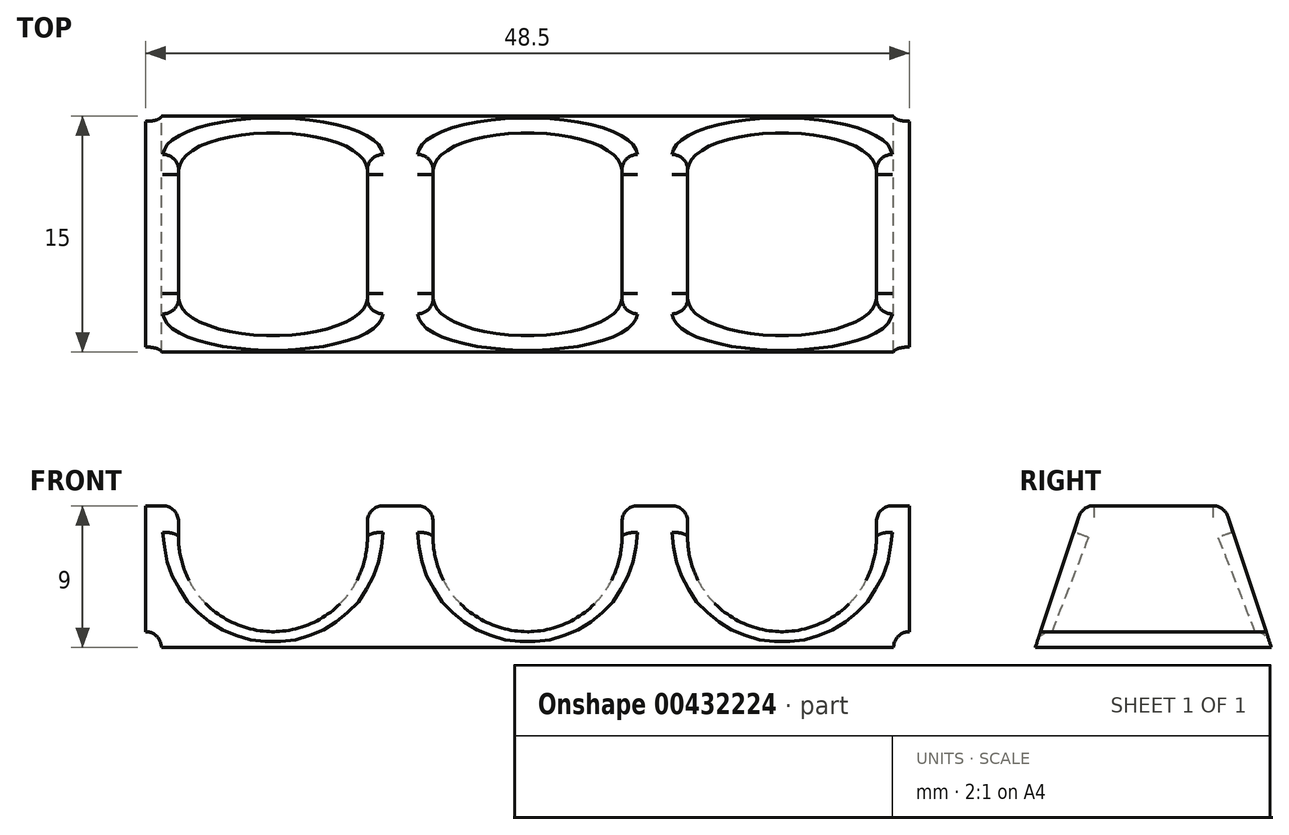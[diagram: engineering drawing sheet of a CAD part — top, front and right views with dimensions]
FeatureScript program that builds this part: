
annotation { "Feature Type Name" : "Feature", "Feature Type Description" : "" }
export const myFeature = defineFeature(function(context is Context, id is Id, definition is map)
    precondition{}
    {
        {
            var Q0;
            Q0=qCreatedBy(makeId("Front.planeOp"),FACE);
            var sketch = newSketch(context, id + "F0", { "sketchPlane" : qUnion([Q0])});
            skLineSegment(sketch, "E0.bottom", {"start": v(24.25, 4.5) * mm, "end": v(22.17, 4.5) * mm});
            skLineSegment(sketch, "E0.top", {"start": v(23.25, -4.5) * mm, "end": v(-23.25, -4.5) * mm});
            skLineSegment(sketch, "E0.left", {"start": v(24.25, 4.5) * mm, "end": v(24.25, -3.5) * mm});
            skLineSegment(sketch, "E0.right", {"start": v(-24.25, 4.5) * mm, "end": v(-24.25, -3.5) * mm});
            skPoint(sketch, "E0.middle", {"position": v(0, 0) * mm});
            skArc(sketch, "E1", {"start": v(-23.25, -4.5) * mm, "mid": v(-23.54, -3.8) * mm, "end": v(-24.25, -3.5) * mm});
            skArc(sketch, "E2", {"start": v(24.25, -3.5) * mm, "mid": v(23.54, -3.8) * mm, "end": v(23.25, -4.5) * mm});
            skArc(sketch, "E3", {"start": v(-22.17, 2.5) * mm, "mid": v(-16.17, -3.5) * mm, "end": v(-10.17, 2.5) * mm});
            skArc(sketch, "E4", {"start": v(10.17, 2.5) * mm, "mid": v(16.17, -3.5) * mm, "end": v(22.17, 2.5) * mm});
            skArc(sketch, "E5", {"start": v(-6, 2.5) * mm, "mid": v(0, -3.5) * mm, "end": v(6, 2.5) * mm});
            skLineSegment(sketch, "E6", {"start": v(-22.17, 2.5) * mm, "end": v(-22.17, 4.5) * mm});
            skLineSegment(sketch, "E7", {"start": v(-10.17, 2.5) * mm, "end": v(-10.17, 4.5) * mm});
            skLineSegment(sketch, "E8", {"start": v(-6, 2.5) * mm, "end": v(-6, 4.5) * mm});
            skLineSegment(sketch, "E9", {"start": v(6, 2.5) * mm, "end": v(6, 4.5) * mm});
            skLineSegment(sketch, "E10", {"start": v(10.17, 2.5) * mm, "end": v(10.17, 4.5) * mm});
            skLineSegment(sketch, "E11", {"start": v(22.17, 2.5) * mm, "end": v(22.17, 4.5) * mm});
            skLineSegment(sketch, "E12.trimOffspring", {"start": v(-22.17, 4.5) * mm, "end": v(-24.25, 4.5) * mm});
            skLineSegment(sketch, "E13.trimOffspring", {"start": v(-6, 4.5) * mm, "end": v(-10.17, 4.5) * mm});
            skLineSegment(sketch, "E14.trimOffspring", {"start": v(10.17, 4.5) * mm, "end": v(6, 4.5) * mm});
            skSolve(sketch);
        }
        {
            var Q0;
            Q0 = qSketchRegion(id + "F0", true);
            extrude(context, id + "F1", {"entities" : qUnion([Q0]), "depth" : 15 * mm});
        }
        {
            var Q0;
            Q0=makeQuery(id+"F1.opExtrude","SWEPT_FACE",FACE,{"disambiguationData":[OSD([sQuery(id+"F0.wireOp",EDGE,"E0.left")])]});
            var sketch = newSketch(context, id + "F2", { "sketchPlane" : qUnion([Q0])});
            skLineSegment(sketch, "E15", {"start": v(-15, 4.5) * mm, "end": v(-12, 4.5) * mm});
            skLineSegment(sketch, "E16", {"start": v(0, 4.5) * mm, "end": v(-3, 4.5) * mm});
            skLineSegment(sketch, "E17", {"start": v(-15, 4.5) * mm, "end": v(-15, -4.5) * mm});
            skLineSegment(sketch, "E18", {"start": v(-15, -4.5) * mm, "end": v(-12, 4.5) * mm});
            skLineSegment(sketch, "E19", {"start": v(0, 4.5) * mm, "end": v(0, -4.5) * mm});
            skLineSegment(sketch, "E20", {"start": v(0, -4.5) * mm, "end": v(-3, 4.5) * mm});
            skSolve(sketch);
        }
        {
            var Q0;
            Q0 = qSketchRegion(id + "F2", true);
            extrude(context, id + "F3", {"entities" : qUnion([Q0]), "operationType" : NewBodyOperationType.REMOVE, "endBound" : BoundingType.THROUGH_ALL, "oppositeDirection" : true, "depth" : 25 * mm});
        }
        {
            var Q0;
            Q0=makeQuery(id+"F1.opExtrude","SWEPT_EDGE",EDGE,{"disambiguationData":[OSD([sQuery(id+"F0.wireOp",EDGE,"E10"),sQuery(id+"F0.wireOp",EDGE,"E14.trimOffspring")])]});
            var Q1;
            Q1=makeQuery(id+"F1.opExtrude","SWEPT_EDGE",EDGE,{"disambiguationData":[OSD([sQuery(id+"F0.wireOp",EDGE,"E9"),sQuery(id+"F0.wireOp",EDGE,"E14.trimOffspring")])]});
            var Q2;
            Q2=makeQuery(id+"F1.opExtrude","SWEPT_EDGE",EDGE,{"disambiguationData":[OSD([sQuery(id+"F0.wireOp",EDGE,"E8"),sQuery(id+"F0.wireOp",EDGE,"E13.trimOffspring")])]});
            var Q3;
            Q3=makeQuery(id+"F1.opExtrude","SWEPT_EDGE",EDGE,{"disambiguationData":[OSD([sQuery(id+"F0.wireOp",EDGE,"E7"),sQuery(id+"F0.wireOp",EDGE,"E13.trimOffspring")])]});
            var Q4;
            Q4=makeQuery(id+"F1.opExtrude","SWEPT_EDGE",EDGE,{"disambiguationData":[OSD([sQuery(id+"F0.wireOp",EDGE,"E6"),sQuery(id+"F0.wireOp",EDGE,"E12.trimOffspring")])]});
            var Q5;
            Q5=makeQuery(id+"F1.opExtrude","SWEPT_EDGE",EDGE,{"disambiguationData":[OSD([sQuery(id+"F0.wireOp",EDGE,"E0.bottom"),sQuery(id+"F0.wireOp",EDGE,"E11")])]});
            fillet(context, id + "F4", {"entities" : qUnion([Q0, Q1, Q2, Q3, Q4, Q5]), "radius" : 1 * mm, "tangentPropagation" : true, "allowEdgeOverflow" : false});
        }
        {
            var Q0;
            Q0=makeQuery(id+"F3.boolean.opBoolean","INTERSECT",EDGE,{"derivedFrom":[makeQuery(id+"F1.opExtrude","SWEPT_FACE",FACE,{"disambiguationData":[OSD([sQuery(id+"F0.wireOp",EDGE,"E4")])]}),makeQuery(id+"F3.opExtrude","SWEPT_FACE",FACE,{"disambiguationData":[OSD([sQuery(id+"F2.wireOp",EDGE,"E20")])]})]});
            var Q1;
            Q1=makeQuery(id+"F3.boolean.opBoolean","INTERSECT",EDGE,{"derivedFrom":[makeQuery(id+"F1.opExtrude","SWEPT_FACE",FACE,{"disambiguationData":[OSD([sQuery(id+"F0.wireOp",EDGE,"E5")])]}),makeQuery(id+"F3.opExtrude","SWEPT_FACE",FACE,{"disambiguationData":[OSD([sQuery(id+"F2.wireOp",EDGE,"E18")])]})]});
            fillet(context, id + "F5", {"entities" : qUnion([Q0, Q1]), "radius" : 1 * mm, "tangentPropagation" : true, "allowEdgeOverflow" : false});
        }
    });
